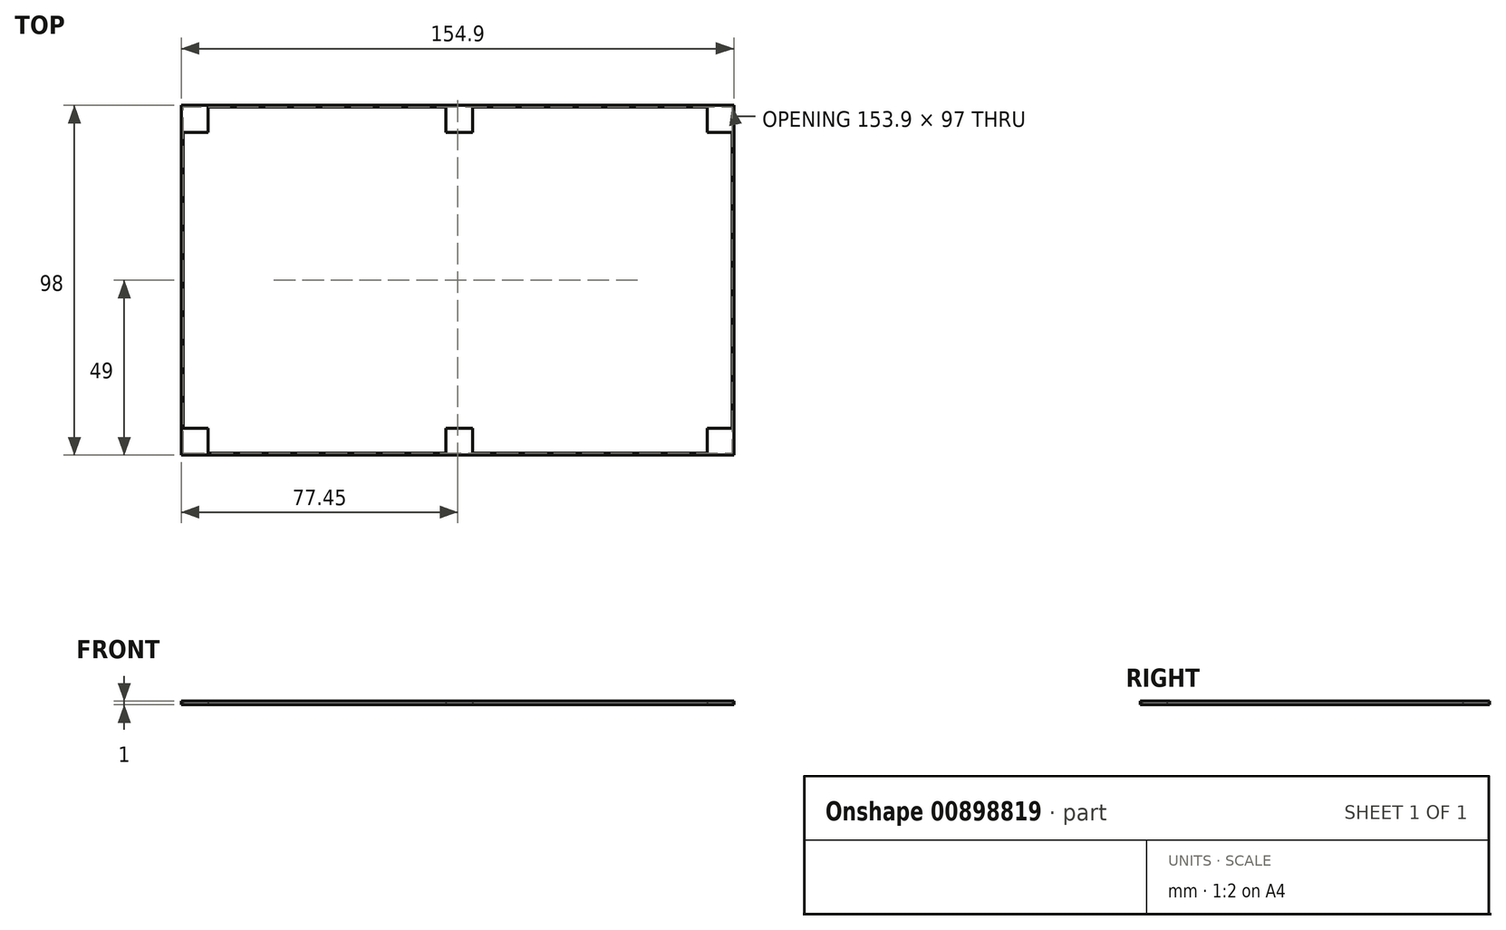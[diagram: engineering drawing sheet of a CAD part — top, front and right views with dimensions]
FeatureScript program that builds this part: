
annotation { "Feature Type Name" : "Feature", "Feature Type Description" : "" }
export const myFeature = defineFeature(function(context is Context, id is Id, definition is map)
    precondition{}
    {
        {
            var Q0;
            Q0=qCreatedBy(makeId("Top.planeOp"),FACE);
            var sketch = newSketch(context, id + "F0", { "sketchPlane" : qUnion([Q0])});
            skLineSegment(sketch, "E0.bottom", {"start": v(-77.45, 49) * mm, "end": v(77.45, 49) * mm});
            skLineSegment(sketch, "E0.top", {"start": v(-77.45, -49) * mm, "end": v(77.45, -49) * mm});
            skLineSegment(sketch, "E0.left", {"start": v(-77.45, 49) * mm, "end": v(-77.45, -49) * mm});
            skLineSegment(sketch, "E0.right", {"start": v(77.45, 49) * mm, "end": v(77.45, -49) * mm});
            skPoint(sketch, "E0.middle", {"position": v(0, 0) * mm});
            skLineSegment(sketch, "E1.bottom", {"start": v(-77.45, 49) * mm, "end": v(-69.95, 49) * mm});
            skLineSegment(sketch, "E1.top", {"start": v(-77.45, 41.5) * mm, "end": v(-69.95, 41.5) * mm});
            skLineSegment(sketch, "E1.left", {"start": v(-77.45, 49) * mm, "end": v(-77.45, 41.5) * mm});
            skLineSegment(sketch, "E1.right", {"start": v(-69.95, 49) * mm, "end": v(-69.95, 41.5) * mm});
            skLineSegment(sketch, "E2", {"start": v(0, 49) * mm, "end": v(-3.25, 49) * mm});
            skLineSegment(sketch, "E3.bottom", {"start": v(-3.25, 49) * mm, "end": v(4.25, 49) * mm});
            skLineSegment(sketch, "E3.top", {"start": v(-3.25, 41.5) * mm, "end": v(4.25, 41.5) * mm});
            skLineSegment(sketch, "E3.left", {"start": v(-3.25, 49) * mm, "end": v(-3.25, 41.5) * mm});
            skLineSegment(sketch, "E3.right", {"start": v(4.25, 49) * mm, "end": v(4.25, 41.5) * mm});
            skLineSegment(sketch, "E4.bottom", {"start": v(77.45, 49) * mm, "end": v(69.95, 49) * mm});
            skLineSegment(sketch, "E4.top", {"start": v(77.45, 41.5) * mm, "end": v(69.95, 41.5) * mm});
            skLineSegment(sketch, "E4.left", {"start": v(77.45, 49) * mm, "end": v(77.45, 41.5) * mm});
            skLineSegment(sketch, "E4.right", {"start": v(69.95, 49) * mm, "end": v(69.95, 41.5) * mm});
            skLineSegment(sketch, "E5.MirrorCS", {"start": v(0, -49) * mm, "end": v(-3.25, -49) * mm});
            skLineSegment(sketch, "E6.MirrorCS", {"start": v(-3.25, -49) * mm, "end": v(4.25, -49) * mm});
            skLineSegment(sketch, "E7.MirrorCS", {"start": v(77.45, -41.5) * mm, "end": v(69.95, -41.5) * mm});
            skLineSegment(sketch, "E8.MirrorCS", {"start": v(-3.25, -49) * mm, "end": v(-3.25, -41.5) * mm});
            skLineSegment(sketch, "E9.MirrorCS", {"start": v(-69.95, -49) * mm, "end": v(-69.95, -41.5) * mm});
            skLineSegment(sketch, "E10.MirrorCS", {"start": v(-77.45, -49) * mm, "end": v(-69.95, -49) * mm});
            skLineSegment(sketch, "E11.MirrorCS", {"start": v(77.45, -49) * mm, "end": v(77.45, -41.5) * mm});
            skLineSegment(sketch, "E12.MirrorCS", {"start": v(69.95, -49) * mm, "end": v(69.95, -41.5) * mm});
            skLineSegment(sketch, "E13.MirrorCS", {"start": v(-77.45, -41.5) * mm, "end": v(-69.95, -41.5) * mm});
            skLineSegment(sketch, "E14.MirrorCS", {"start": v(4.25, -49) * mm, "end": v(4.25, -41.5) * mm});
            skLineSegment(sketch, "E15.MirrorCS", {"start": v(77.45, -49) * mm, "end": v(69.95, -49) * mm});
            skLineSegment(sketch, "E16.MirrorCS", {"start": v(-3.25, -41.5) * mm, "end": v(4.25, -41.5) * mm});
            skLineSegment(sketch, "E17.MirrorCS", {"start": v(-77.45, -49) * mm, "end": v(-77.45, -41.5) * mm});
            skLineSegment(sketch, "E18", {"start": v(-77.45, 41.5) * mm, "end": v(-76.95, 41.5) * mm});
            skLineSegment(sketch, "E19", {"start": v(-76.95, 41.5) * mm, "end": v(-76.95, -41.5) * mm});
            skLineSegment(sketch, "E20", {"start": v(-69.95, -49) * mm, "end": v(-69.95, -48.5) * mm});
            skLineSegment(sketch, "E21", {"start": v(-69.95, -48.5) * mm, "end": v(-3.25, -48.5) * mm});
            skLineSegment(sketch, "E22", {"start": v(4.25, -49) * mm, "end": v(4.25, -48.5) * mm});
            skLineSegment(sketch, "E23", {"start": v(4.25, -48.5) * mm, "end": v(69.95, -48.5) * mm});
            skLineSegment(sketch, "E24", {"start": v(77.45, -41.5) * mm, "end": v(76.95, -41.5) * mm});
            skLineSegment(sketch, "E25", {"start": v(76.95, -41.5) * mm, "end": v(76.95, 41.5) * mm});
            skLineSegment(sketch, "E26", {"start": v(-69.95, 49) * mm, "end": v(-69.95, 48.5) * mm});
            skLineSegment(sketch, "E27", {"start": v(-69.95, 48.5) * mm, "end": v(-3.25, 48.5) * mm});
            skLineSegment(sketch, "E28", {"start": v(4.25, 49) * mm, "end": v(4.25, 48.5) * mm});
            skLineSegment(sketch, "E29", {"start": v(4.25, 48.5) * mm, "end": v(69.95, 48.5) * mm});
            skPoint(sketch, "E29.endSnap0", {"position": v(69.95, 45.25) * mm});
            skSolve(sketch);
        }
        {
            var Q0;
            Q0 = qSketchRegion(id + "F0", true);
            extrude(context, id + "F1", {"entities" : qUnion([Q0]), "depth" : 1 * mm, "offsetDistance" : 25 * mm});
        }
    });
